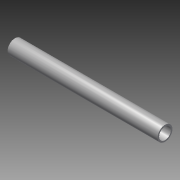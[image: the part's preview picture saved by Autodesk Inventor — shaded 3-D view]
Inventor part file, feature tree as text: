
AUTODESK INVENTOR PART (.ipt)
format: ipt  version: 2014 (Build 180170000, 170)  size: 100,864 bytes
history: native  units: in
note: dims shown in document units (in); Inventor stores cm internally (conversion verified against a paired STEP export)
features: other x2, extrude x1, imported_body x1, sketch x1
ambient origin geometry x8: Origin, YZ Plane, XZ Plane, XY Plane, X Axis, Y Axis, Z Axis, Center Point
bodies: Body1 (feature_tree)
feature tree (5):
  parser-record x1  (decoder bookkeeping rows leaked as tree rows — omitted from the tree; the rows remain in map.json)
  other  "4347K3111"
  extrude  "Extrusion2"  [1 undecoded]
  imported_body  "Base1"
  sketch  "Sketch2"  dims[d2=3.5in d3=0.0in]
note: 1 required parameter value undecoded (feature->parameter linkage not recoverable at this tier; creation-order binding heuristic only, values carry confidence <= 0.55)
